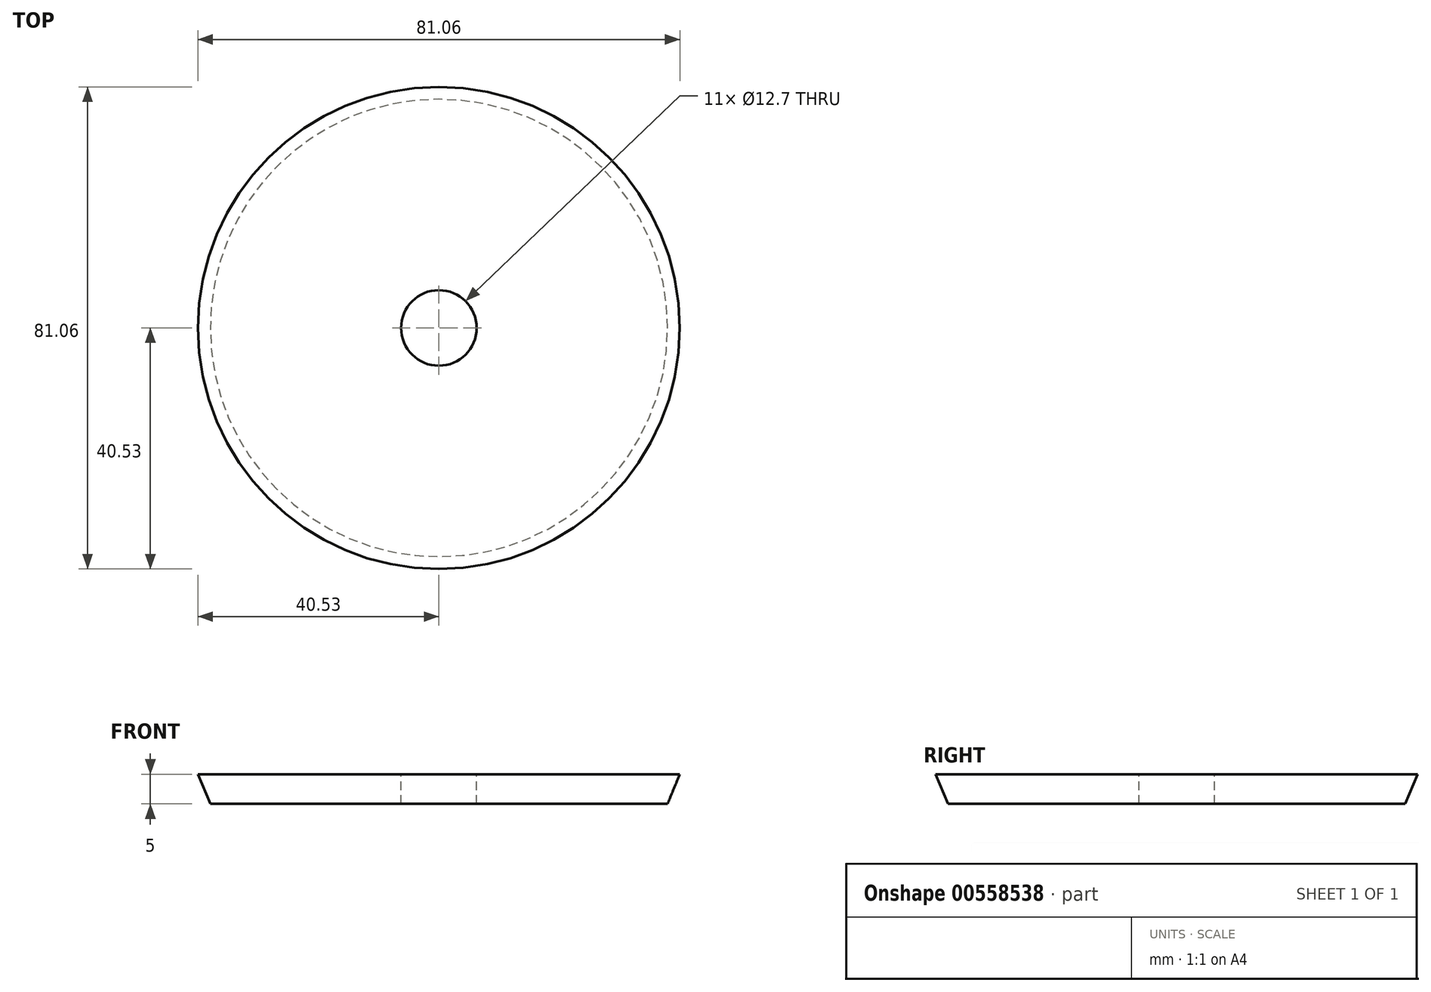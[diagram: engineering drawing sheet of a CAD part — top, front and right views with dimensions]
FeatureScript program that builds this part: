
annotation { "Feature Type Name" : "Feature", "Feature Type Description" : "" }
export const myFeature = defineFeature(function(context is Context, id is Id, definition is map)
    precondition{}
    {
        {
            var Q0;
            Q0=qCreatedBy(makeId("Top.planeOp"),FACE);
            var sketch = newSketch(context, id + "F0", { "sketchPlane" : qUnion([Q0])});
            skCircle(sketch, "E0", {"center": v(0, 0) * mm, "radius": 50.8 * mm});
            skSolve(sketch);
        }
        {
            var Q0;
            Q0=makeQuery(id+"F0.imprint","IMPRINT",FACE,{"disambiguationData":[TD([[makeQuery(id+"F0.imprint","IMPRINT",EDGE,{"derivedFrom":sQuery(id+"F0.wireOp",EDGE,"E0")}),1.0]])]});
            extrude(context, id + "F1", {"entities" : qUnion([Q0]), "depth" : 5 * mm, "offsetDistance" : 25.4 * mm});
        }
        {
            var Q0;
            Q0=makeQuery(id+"F1.opExtrude","CAP_FACE",FACE,{"disambiguationData":[OSD([sQuery(id+"F0.wireOp",EDGE,"E0")])],"isStart":false});
            var sketch = newSketch(context, id + "F2", { "sketchPlane" : qUnion([Q0])});
            skCircle(sketch, "E1", {"center": v(0, 0) * mm, "radius": 6.35 * mm});
            skLineSegment(sketch, "E2", {"start": v(9.83, -56.22) * mm, "end": v(9.66, -49.87) * mm});
            skSolve(sketch);
        }
        {
            var Q0;
            Q0=makeQuery(id+"F2.imprint","IMPRINT",FACE,{"disambiguationData":[TD([[makeQuery(id+"F2.imprint","IMPRINT",EDGE,{"derivedFrom":sQuery(id+"F2.wireOp",EDGE,"E1")}),1.0]])]});
            extrude(context, id + "F3", {"entities" : qUnion([Q0]), "operationType" : NewBodyOperationType.REMOVE, "endBound" : BoundingType.THROUGH_ALL, "oppositeDirection" : true, "depth" : 25.4 * mm, "offsetDistance" : 25.4 * mm});
        }
        {
            var Q0;
            Q0=makeQuery(id+"F1.opExtrude","CAP_EDGE",EDGE,{"disambiguationData":[OSD([sQuery(id+"F0.wireOp",EDGE,"E0")])],"isStart":false});
            chamfer(context, id + "F4", {"entities" : qUnion([Q0]), "width" : 5.08 * mm, "tangentPropagation" : true});
        }
        {
            var Q0;
            {var subQ0=sQuery(id+"F0.wireOp",EDGE,"E0");Q0=makeQuery(id+"F4.opChamfer","BLEND_EDGE",EDGE,{"blendedFrom":[makeQuery(id+"F1.opExtrude","CAP_EDGE",EDGE,{"disambiguationData":[OSD([subQ0])],"isStart":false}),makeQuery(id+"F1.opExtrude","CAP_FACE",FACE,{"disambiguationData":[OSD([subQ0])],"isStart":true})],"blendedInto":[makeQuery(id+"F1.opExtrude","CAP_FACE",FACE,{"disambiguationData":[OSD([subQ0])],"isStart":true})]});}
            chamfer(context, id + "F5", {"entities" : qUnion([Q0]), "width" : 5.08 * mm, "tangentPropagation" : true});
        }
    });
